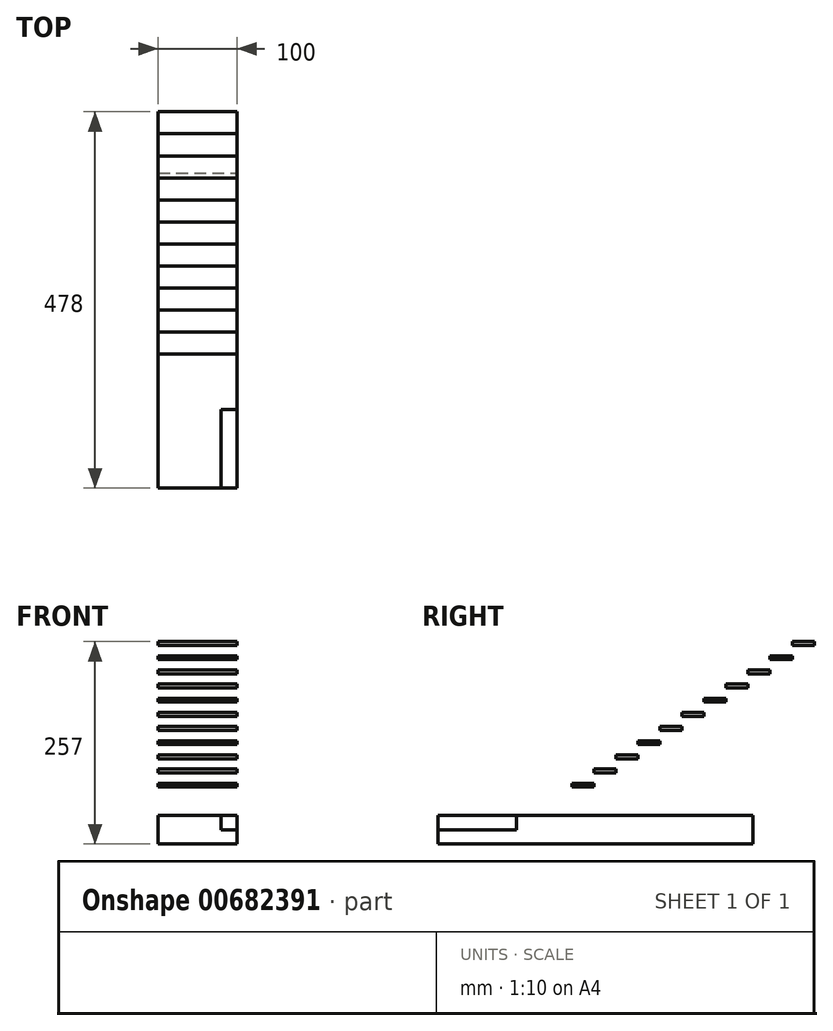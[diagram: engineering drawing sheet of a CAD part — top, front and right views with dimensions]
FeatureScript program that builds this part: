
annotation { "Feature Type Name" : "Feature", "Feature Type Description" : "" }
export const myFeature = defineFeature(function(context is Context, id is Id, definition is map)
    precondition{}
    {
        {
            var Q0;
            Q0=qCreatedBy(makeId("Right.planeOp"),FACE);
            var sketch = newSketch(context, id + "F0", { "sketchPlane" : qUnion([Q0])});
            skLineSegment(sketch, "E0.top", {"start": v(0, 0) * mm, "end": v(-250, 0) * mm});
            skLineSegment(sketch, "E1.bottom", {"start": v(-250, 0) * mm, "end": v(150, 0) * mm});
            skLineSegment(sketch, "E1.top", {"start": v(-250, 36) * mm, "end": v(150, 36) * mm});
            skLineSegment(sketch, "E1.left", {"start": v(-250, 0) * mm, "end": v(-250, 36) * mm});
            skLineSegment(sketch, "E1.right", {"start": v(150, 0) * mm, "end": v(150, 36) * mm});
            skLineSegment(sketch, "E2.bottom", {"start": v(-250, 36) * mm, "end": v(-50, 36) * mm});
            skLineSegment(sketch, "E2.top", {"start": v(-250, 54) * mm, "end": v(-0.07, 54) * mm});
            skLineSegment(sketch, "E2.left", {"start": v(-250, 36) * mm, "end": v(-250, 54) * mm});
            skLineSegment(sketch, "E2.right", {"start": v(-50, 36) * mm, "end": v(-50, 54) * mm});
            skLineSegment(sketch, "E3.bottom", {"start": v(-250, 54) * mm, "end": v(-50, 54) * mm});
            skSolve(sketch);
        }
        {
            var Q0;
            Q0=makeQuery(id+"F0.imprint","IMPRINT",FACE,{"disambiguationData":[TD([[makeQuery(id+"F0.imprint","IMPRINT",EDGE,{"derivedFrom":sQuery(id+"F0.wireOp",EDGE,"E1.top")}),-1.0]])]});
            var Q1;
            Q1=makeQuery(id+"F0.imprint","IMPRINT",FACE,{"disambiguationData":[TD([[makeQuery(id+"F0.imprint","IMPRINT",EDGE,{"derivedFrom":sQuery(id+"F0.wireOp",EDGE,"E2.bottom")}),1.0]])]});
            extrude(context, id + "F1", {"entities" : qUnion([Q0, Q1]), "oppositeDirection" : true, "depth" : 80 * mm, "offsetDistance" : 25 * mm});
        }
        {
            var Q0;
            Q0=makeQuery(id+"F1.opExtrude","CAP_FACE",FACE,{"disambiguationData":[OSD([sQuery(id+"F0.wireOp",EDGE,"E0.bottom"),sQuery(id+"F0.wireOp",EDGE,"E0.top"),sQuery(id+"F0.wireOp",EDGE,"E0.left"),sQuery(id+"F0.wireOp",EDGE,"E0.right"),sQuery(id+"F0.wireOp",EDGE,"E1.top"),sQuery(id+"F0.wireOp",EDGE,"E1.left"),sQuery(id+"F0.wireOp",EDGE,"E1.right"),sQuery(id+"F0.wireOp",EDGE,"E2.top"),sQuery(id+"F0.wireOp",EDGE,"E2.left"),sQuery(id+"F0.wireOp",EDGE,"E2.right"),sQuery(id+"F0.wireOp",EDGE,"E3.top"),sQuery(id+"F0.wireOp",EDGE,"E3.left"),sQuery(id+"F0.wireOp",EDGE,"E3.right"),sQuery(id+"F0.wireOp",EDGE,"yrYCP7ny-YcMI-JWOk-0YpH-LF2ZJ5aTu4Mx.top"),sQuery(id+"F0.wireOp",EDGE,"yrYCP7ny-YcMI-JWOk-0YpH-LF2ZJ5aTu4Mx.left"),sQuery(id+"F0.wireOp",EDGE,"yrYCP7ny-YcMI-JWOk-0YpH-LF2ZJ5aTu4Mx.right")])],"isStart":true});
            var sketch = newSketch(context, id + "F2", { "sketchPlane" : qUnion([Q0])});
            skPoint(sketch, "E4.orphan", {"position": v(0, 90) * mm});
            skPoint(sketch, "E5.orphan", {"position": v(0, 0) * mm});
            skLineSegment(sketch, "E6.bottom", {"start": v(-250, 0) * mm, "end": v(-150, 0) * mm});
            skLineSegment(sketch, "E6.top", {"start": v(-250, 18) * mm, "end": v(-150, 18) * mm});
            skLineSegment(sketch, "E6.left", {"start": v(-250, 0) * mm, "end": v(-250, 18) * mm});
            skLineSegment(sketch, "E6.right", {"start": v(-150, 0) * mm, "end": v(-150, 18) * mm});
            skSolve(sketch);
        }
        {
            var Q0;
            Q0 = qSketchRegion(id + "F2", true);
            extrude(context, id + "F3", {"entities" : qUnion([Q0]), "operationType" : NewBodyOperationType.ADD, "depth" : 20 * mm, "offsetDistance" : 25 * mm});
        }
        {
            var Q0;
            Q0=qCreatedBy(makeId("Right.planeOp"),FACE);
            var sketch = newSketch(context, id + "F4", { "sketchPlane" : qUnion([Q0])});
            skLineSegment(sketch, "E7", {"start": v(-80, 72) * mm, "end": v(-52, 72) * mm});
            skLineSegment(sketch, "E8", {"start": v(-52, 72) * mm, "end": v(-52, 90) * mm, "construction": true});
            skLineSegment(sketch, "E9", {"start": v(-52, 90) * mm, "end": v(-24, 90) * mm});
            skLineSegment(sketch, "E10", {"start": v(-24, 90) * mm, "end": v(-24, 108) * mm, "construction": true});
            skLineSegment(sketch, "E11", {"start": v(-24, 108) * mm, "end": v(4, 108) * mm});
            skLineSegment(sketch, "E12", {"start": v(4, 108) * mm, "end": v(4, 126) * mm, "construction": true});
            skLineSegment(sketch, "E13", {"start": v(4, 126) * mm, "end": v(32, 126) * mm});
            skLineSegment(sketch, "E14", {"start": v(32, 126) * mm, "end": v(32, 144) * mm, "construction": true});
            skLineSegment(sketch, "E15", {"start": v(32, 144) * mm, "end": v(60, 144) * mm});
            skLineSegment(sketch, "E16", {"start": v(60, 144) * mm, "end": v(60, 162) * mm, "construction": true});
            skLineSegment(sketch, "E17", {"start": v(60, 162) * mm, "end": v(88, 162) * mm});
            skLineSegment(sketch, "E18", {"start": v(88, 162) * mm, "end": v(88, 180) * mm, "construction": true});
            skLineSegment(sketch, "E19", {"start": v(88, 180) * mm, "end": v(116, 180) * mm});
            skLineSegment(sketch, "E20", {"start": v(116, 180) * mm, "end": v(116, 198) * mm, "construction": true});
            skLineSegment(sketch, "E21", {"start": v(116, 198) * mm, "end": v(144, 198) * mm});
            skLineSegment(sketch, "E22", {"start": v(144, 198) * mm, "end": v(144, 216) * mm, "construction": true});
            skLineSegment(sketch, "E23", {"start": v(144, 216) * mm, "end": v(172, 216) * mm});
            skLineSegment(sketch, "E24", {"start": v(172, 216) * mm, "end": v(172, 234) * mm, "construction": true});
            skLineSegment(sketch, "E25", {"start": v(172, 234) * mm, "end": v(200, 234) * mm});
            skLineSegment(sketch, "E26", {"start": v(200, 234) * mm, "end": v(200, 252) * mm, "construction": true});
            skLineSegment(sketch, "E27", {"start": v(200, 252) * mm, "end": v(228, 252) * mm});
            skLineSegment(sketch, "E28.0.1.0", {"start": v(200, 239) * mm, "end": v(200, 257) * mm, "construction": true});
            skLineSegment(sketch, "E28.0.1.1", {"start": v(172, 221) * mm, "end": v(172, 239) * mm, "construction": true});
            skLineSegment(sketch, "E28.0.1.2", {"start": v(116, 185) * mm, "end": v(116, 203) * mm, "construction": true});
            skLineSegment(sketch, "E28.0.1.3", {"start": v(4, 131) * mm, "end": v(32, 131) * mm});
            skLineSegment(sketch, "E28.0.1.4", {"start": v(172, 239) * mm, "end": v(200, 239) * mm});
            skLineSegment(sketch, "E28.0.1.5", {"start": v(200, 257) * mm, "end": v(228, 257) * mm});
            skLineSegment(sketch, "E28.0.1.6", {"start": v(116, 203) * mm, "end": v(144, 203) * mm});
            skLineSegment(sketch, "E28.0.1.7", {"start": v(88, 185) * mm, "end": v(116, 185) * mm});
            skLineSegment(sketch, "E28.0.1.8", {"start": v(88, 167) * mm, "end": v(88, 185) * mm, "construction": true});
            skLineSegment(sketch, "E28.0.1.9", {"start": v(60, 167) * mm, "end": v(88, 167) * mm});
            skLineSegment(sketch, "E28.0.1.10", {"start": v(144, 203) * mm, "end": v(144, 221) * mm, "construction": true});
            skLineSegment(sketch, "E28.0.1.11", {"start": v(60, 149) * mm, "end": v(60, 167) * mm, "construction": true});
            skLineSegment(sketch, "E28.0.1.12", {"start": v(-80, 77) * mm, "end": v(-52, 77) * mm});
            skLineSegment(sketch, "E28.0.1.13", {"start": v(32, 149) * mm, "end": v(60, 149) * mm});
            skLineSegment(sketch, "E28.0.1.14", {"start": v(144, 221) * mm, "end": v(172, 221) * mm});
            skLineSegment(sketch, "E28.0.1.15", {"start": v(-52, 77) * mm, "end": v(-52, 95) * mm, "construction": true});
            skLineSegment(sketch, "E28.0.1.16", {"start": v(-52, 95) * mm, "end": v(-24, 95) * mm});
            skLineSegment(sketch, "E28.0.1.17", {"start": v(32, 131) * mm, "end": v(32, 149) * mm, "construction": true});
            skLineSegment(sketch, "E28.0.1.18", {"start": v(-24, 95) * mm, "end": v(-24, 113) * mm, "construction": true});
            skLineSegment(sketch, "E28.0.1.19", {"start": v(-24, 113) * mm, "end": v(4, 113) * mm});
            skLineSegment(sketch, "E28.0.1.20", {"start": v(4, 113) * mm, "end": v(4, 131) * mm, "construction": true});
            skLineSegment(sketch, "E28.direction1", {"start": v(-80, 72) * mm, "end": v(-7.96, 72) * mm, "construction": true});
            skLineSegment(sketch, "E28.direction2", {"start": v(-80, 72) * mm, "end": v(-80, 77) * mm, "construction": true});
            skLineSegment(sketch, "E29", {"start": v(228, 257) * mm, "end": v(228, 252) * mm});
            skLineSegment(sketch, "E30", {"start": v(200, 257) * mm, "end": v(200, 252) * mm});
            skLineSegment(sketch, "E31", {"start": v(200, 239) * mm, "end": v(200, 234) * mm});
            skLineSegment(sketch, "E32", {"start": v(172, 239) * mm, "end": v(172, 234) * mm});
            skLineSegment(sketch, "E33", {"start": v(172, 221) * mm, "end": v(172, 216) * mm});
            skLineSegment(sketch, "E34", {"start": v(144, 221) * mm, "end": v(144, 216) * mm});
            skLineSegment(sketch, "E35", {"start": v(144, 203) * mm, "end": v(144, 198) * mm});
            skLineSegment(sketch, "E36", {"start": v(116, 203) * mm, "end": v(116, 198) * mm});
            skLineSegment(sketch, "E37", {"start": v(116, 185) * mm, "end": v(116, 180) * mm});
            skLineSegment(sketch, "E38", {"start": v(88, 185) * mm, "end": v(88, 180) * mm});
            skLineSegment(sketch, "E39", {"start": v(88, 167) * mm, "end": v(88, 162) * mm});
            skLineSegment(sketch, "E40", {"start": v(60, 167) * mm, "end": v(60, 162) * mm});
            skLineSegment(sketch, "E41", {"start": v(60, 149) * mm, "end": v(60, 144) * mm});
            skLineSegment(sketch, "E42", {"start": v(32, 149) * mm, "end": v(32, 144) * mm});
            skLineSegment(sketch, "E43", {"start": v(32, 131) * mm, "end": v(32, 126) * mm});
            skLineSegment(sketch, "E44", {"start": v(4, 131) * mm, "end": v(4, 126) * mm});
            skLineSegment(sketch, "E45", {"start": v(4, 113) * mm, "end": v(4, 108) * mm});
            skLineSegment(sketch, "E46", {"start": v(-24, 113) * mm, "end": v(-24, 108) * mm});
            skLineSegment(sketch, "E47", {"start": v(-24, 95) * mm, "end": v(-24, 90) * mm});
            skLineSegment(sketch, "E48", {"start": v(-52, 95) * mm, "end": v(-52, 90) * mm});
            skLineSegment(sketch, "E49", {"start": v(-52, 77) * mm, "end": v(-52, 72) * mm});
            skLineSegment(sketch, "E50", {"start": v(-80, 77) * mm, "end": v(-80, 72) * mm});
            skSolve(sketch);
        }
        {
            var Q0;
            Q0 = qSketchRegion(id + "F4", true);
            extrude(context, id + "F5", {"entities" : qUnion([Q0]), "oppositeDirection" : true, "depth" : 80 * mm, "offsetDistance" : 25 * mm, "hasSecondDirection" : true, "secondDirectionOppositeDirection" : false, "secondDirectionDepth" : 20 * mm});
        }
        {
            var Q0;
            Q0=qCreatedBy(makeId("Right.planeOp"),FACE);
            var sketch = newSketch(context, id + "F6", { "sketchPlane" : qUnion([Q0])});
            skLineSegment(sketch, "E51.bottom", {"start": v(-250, 54) * mm, "end": v(-150, 54) * mm});
            skLineSegment(sketch, "E51.top", {"start": v(-250, 36) * mm, "end": v(-150, 36) * mm});
            skLineSegment(sketch, "E51.left", {"start": v(-250, 54) * mm, "end": v(-250, 36) * mm});
            skLineSegment(sketch, "E52", {"start": v(-150, 36) * mm, "end": v(-150, 54) * mm});
            skSolve(sketch);
        }
        {
            var Q0;
            Q0=makeQuery(id+"F6.imprint","IMPRINT",FACE,{"disambiguationData":[TD([[makeQuery(id+"F6.imprint","IMPRINT",EDGE,{"derivedFrom":sQuery(id+"F6.wireOp",EDGE,"E51.bottom")}),-1.0]])]});
            extrude(context, id + "F7", {"entities" : qUnion([Q0]), "operationType" : NewBodyOperationType.REMOVE, "oppositeDirection" : true, "depth" : 25 * mm, "offsetDistance" : 25 * mm});
        }
        {
            var Q0;
            Q0=qCreatedBy(makeId("Right.planeOp"),FACE);
            var sketch = newSketch(context, id + "F8", { "sketchPlane" : qUnion([Q0])});
            skLineSegment(sketch, "E53.bottom", {"start": v(-150, 36) * mm, "end": v(150, 36) * mm});
            skLineSegment(sketch, "E53.top", {"start": v(-150, 0) * mm, "end": v(150, 0) * mm});
            skLineSegment(sketch, "E53.left", {"start": v(-150, 36) * mm, "end": v(-150, 0) * mm});
            skLineSegment(sketch, "E53.right", {"start": v(150, 36) * mm, "end": v(150, 0) * mm});
            skSolve(sketch);
        }
        {
            var Q0;
            Q0 = qSketchRegion(id + "F8", true);
            extrude(context, id + "F9", {"entities" : qUnion([Q0]), "operationType" : NewBodyOperationType.ADD, "depth" : 20 * mm, "offsetDistance" : 25 * mm});
        }
    });
